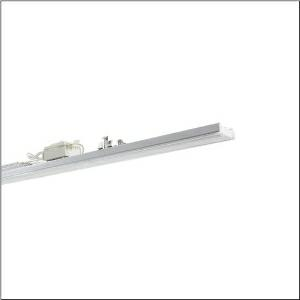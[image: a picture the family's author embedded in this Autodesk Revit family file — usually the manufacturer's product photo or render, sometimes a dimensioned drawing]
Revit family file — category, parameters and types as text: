
# Revit family: licross_r__11_recessed_mo_51te117n485g_c7ea
name_source: partatom
category: Lighting Fixtures
units: mm (PartAtom-declared; Revit-internal decimal feet)

## family parameters
Cut with Voids When Loaded = No
Host = Face
Light Source = No
Part Type = Normal
Room Calculation Point = No
Round Connector Dimension = Use Diameter
Shared = No

## types (1)
- Licross® 11 Recessed MO (1 x LED, 8810 lm, 48.5 W, 4000K)
    Apparent Load = 49 VA
    CIE Flux Codes = 89 96 99 100 100
    Color Rendering = 80
    Color Temperature = 4000K
    Default Elevation = 1800 mm
    Description = Licross® 11 Recessed MO, luminaire insert, of sheet steel, galvanised, coil coated, white, length: 1.500mm, width: 66mm, height: 67mm, LED rated luminous flux: 8.820lm, light colour: 840, control gear: ON/OFF, with plug, 3-pole, with phase selection, mains connection: 220..240V, AC, 50/60Hz, rated input power: 49W, halogen-free wiring, primary light control with lens, of plastic, primary optical cover: cover, of PMMA, light emission: direct distribution, primary light characteristic: symmetric, protection rating (complete): IP54, insulation class (complete): insulation class I (protective earthing), certification: CE, ENEC, VDE, UKCA, protection symbol: D if used in an environment with non-conductive dust loads with corresponding accessories, impact resistance: IK06, permissible ambient temperature for indoor applications: -35..+35°C, corresponds to IFS (International Featured Standards) requirements for safety and quality in the food industry, reducing of maximum allowable ambient temperature of 5°C with ceiling mounting, packaging unit: 1 piece
    Height = 58 mm
    Lamp = 1 x LED
    Lamp Light Flux = 8810 lm
    Lamp Power = 48.5 W
    Lamp count = 1
    Length = 1500 mm
    Luminous efficacy = 182 lm/W
    Manufacturer = Siteco
    ModVariant = No
    Model = 51TE117N485G
    Mounting Place = Ceiling
    Mounting Type = Pendant
    Number of Poles = 1
    OnlyDefault = Yes
    Power Factor = 1
    Product Name = Licross® 11 Recessed MO
    Product group = luminaire insert
    ProductGroupID = 902
    Protection Class = Protection class I
    Protection Degree = IP 54
    RLX_Detail_Level = 1
    RLX_Emergency_Light_Flux = 0 lm
    RLX_Emergency_Type = 0
    RLX_Emergency_Type_DB = No
    RlxData = <blob elided: 20749 chars, md5=2e92eaf2>
    Socket = socket
    Standby Power = 0 W
    System Light Flux = 8810 lm
    System Power = 49 W
    Type Comments = Product without accessories
    Type Image = l_1296930.jpg
    URL = http://relux.com
    VarID = ---
    Voltage = 0 V
    Weight = 0.00 kg
    Width = 66 mm

## geometry (parser evidence)
native form markers: Blend x4, Sweep x12
no freeform markers — native parametric forms only
